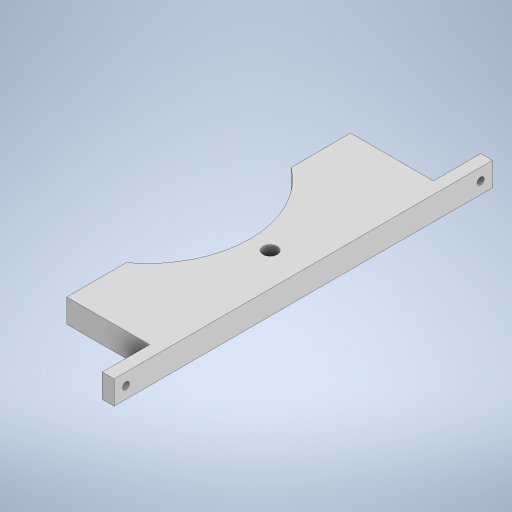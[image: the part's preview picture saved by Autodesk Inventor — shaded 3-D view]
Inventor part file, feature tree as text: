
AUTODESK INVENTOR PART (.ipt)
format: ipt  version: 2023 (Build 270158000, 158)  size: 267,264 bytes
history: native  units: mm
features: extrude x2, thread x2, sketch x2, other x1
ambient origin geometry x8: Origin, YZ Plane, XZ Plane, XY Plane, X Axis, Y Axis, Z Axis, Center Point
bodies: Body1 (feature_tree)
feature tree (7):
  other  "Твердое тело1"
  extrude  "Выдавливание1"  Depth=130.0mm
  extrude  "Выдавливание2"  Depth=120.0mm
  thread  "Резьба1"
  thread  "Резьба2"
  sketch  "Эскиз1"
  sketch  "Эскиз2"
